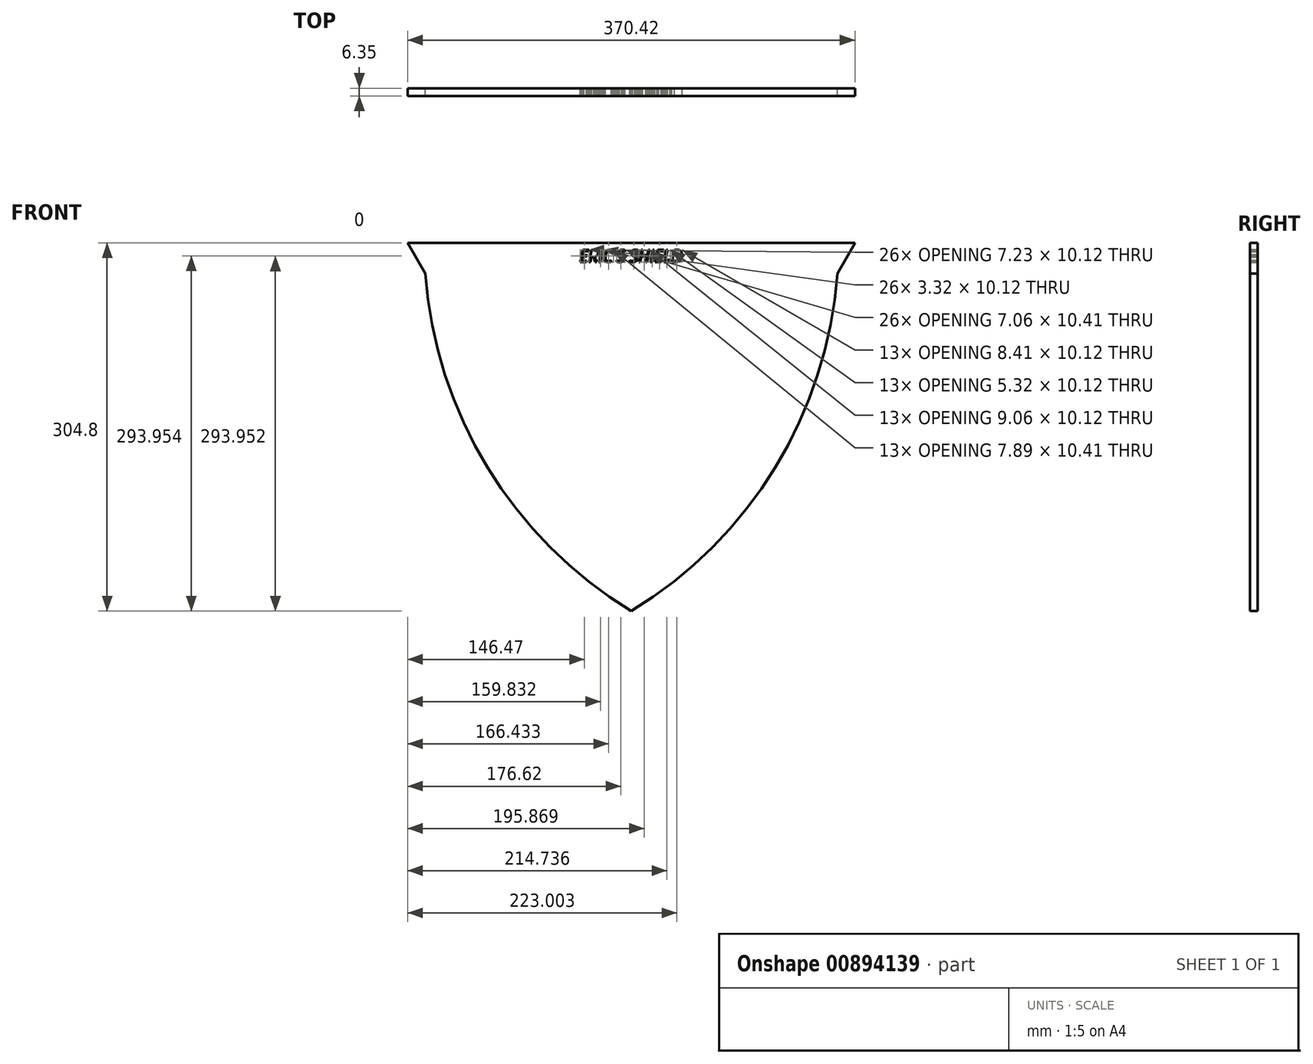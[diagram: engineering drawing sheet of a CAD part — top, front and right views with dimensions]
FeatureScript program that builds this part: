
annotation { "Feature Type Name" : "Feature", "Feature Type Description" : "" }
export const myFeature = defineFeature(function(context is Context, id is Id, definition is map)
    precondition{}
    {
        {
            var Q0;
            Q0=qCreatedBy(makeId("Front.planeOp"),FACE);
            var sketch = newSketch(context, id + "F0", { "sketchPlane" : qUnion([Q0])});
            skLineSegment(sketch, "E0", {"start": v(-170.54, 179.08) * mm, "end": v(170.54, 179.08) * mm});
            skArc(sketch, "E1", {"start": v(-170.54, 179.08) * mm, "mid": v(-119.22, 18.66) * mm, "end": v(0, -100.32) * mm});
            skArc(sketch, "E2", {"start": v(0, -100.32) * mm, "mid": v(119.22, 18.66) * mm, "end": v(170.54, 179.08) * mm});
            skLineSegment(sketch, "E3", {"start": v(-170.54, 179.08) * mm, "end": v(-185.2, 204.48) * mm});
            skLineSegment(sketch, "E4", {"start": v(-185.2, 204.48) * mm, "end": v(185.2, 204.48) * mm});
            skLineSegment(sketch, "E5", {"start": v(170.54, 179.08) * mm, "end": v(185.2, 204.48) * mm});
            skText(sketch, "E6", { "text": "ERIC\'S SHIELD", "fontName": "OpenSans-Italic.ttf"});
            skLineSegment(sketch, "E7", {"start": v(7992.32, 179.08) * mm, "end": v(7992.32, 204.48) * mm});
            const initialGuessF0  = {"E6": [-0.04295, 0.18857, 1, 0, 0.01021]};
            skSetInitialGuess(sketch, initialGuessF0);
            skSolve(sketch);
        }
        {
            var Q0;
            Q0 = qSketchRegion(id + "F0", true);
            extrude(context, id + "F1", {"entities" : qUnion([Q0]), "depth" : 6.35 * mm, "offsetDistance" : 25.4 * mm});
        }
    });
